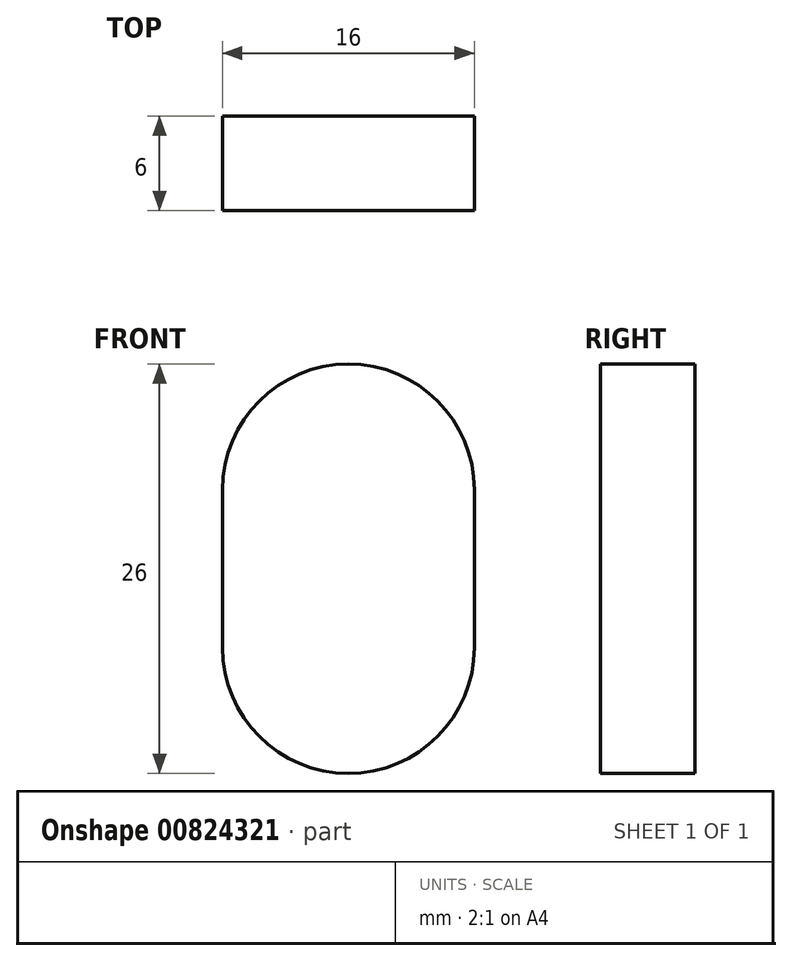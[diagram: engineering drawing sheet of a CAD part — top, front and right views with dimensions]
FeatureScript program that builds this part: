
annotation { "Feature Type Name" : "Feature", "Feature Type Description" : "" }
export const myFeature = defineFeature(function(context is Context, id is Id, definition is map)
    precondition{}
    {
        {
            var Q0;
            Q0=qCreatedBy(makeId("Front.planeOp"),FACE);
            var sketch = newSketch(context, id + "F0", { "sketchPlane" : qUnion([Q0])});
            skLineSegment(sketch, "E0.bottom", {"start": v(130, 80) * mm, "end": v(-130, 80) * mm});
            skLineSegment(sketch, "E0.top", {"start": v(130, -80) * mm, "end": v(-130, -80) * mm});
            skLineSegment(sketch, "E0.left", {"start": v(130, 80) * mm, "end": v(130, -80) * mm});
            skLineSegment(sketch, "E0.right", {"start": v(-130, 80) * mm, "end": v(-130, -80) * mm});
            skPoint(sketch, "E0.middle", {"position": v(0, 0) * mm});
            skSolve(sketch);
        }
        {
            var Q0;
            Q0=makeQuery(id+"F0.imprint","IMPRINT",FACE,{"disambiguationData":[TD([[makeQuery(id+"F0.imprint","IMPRINT",EDGE,{"derivedFrom":sQuery(id+"F0.wireOp",EDGE,"E0.bottom")}),1.0]])]});
            extrude(context, id + "F1", {"entities" : qUnion([Q0]), "depth" : 6 * mm, "offsetDistance" : 25 * mm});
        }
        {
            var Q0;
            Q0=makeQuery(id+"F1.opExtrude","CAP_FACE",FACE,{"disambiguationData":[OSD([sQuery(id+"F0.wireOp",EDGE,"E0.bottom"),sQuery(id+"F0.wireOp",EDGE,"E0.top"),sQuery(id+"F0.wireOp",EDGE,"E0.left"),sQuery(id+"F0.wireOp",EDGE,"E0.right")])],"isStart":false});
            var sketch = newSketch(context, id + "F2", { "sketchPlane" : qUnion([Q0])});
            skLineSegment(sketch, "E1.bottom", {"start": v(-110, -13) * mm, "end": v(-110, -13) * mm});
            skLineSegment(sketch, "E1.top", {"start": v(-110, 13) * mm, "end": v(-110, 13) * mm});
            skLineSegment(sketch, "E1.left", {"start": v(-102, -5) * mm, "end": v(-102, 5) * mm});
            skLineSegment(sketch, "E1.right", {"start": v(-118, -5) * mm, "end": v(-118, 5) * mm});
            skPoint(sketch, "E1.middle", {"position": v(-110, 0) * mm});
            skPoint(sketch, "E2.visualSharp", {"position": v(-118, 13) * mm});
            skArc(sketch, "E2.filletArc", {"start": v(-110, 13) * mm, "mid": v(-115.66, 10.66) * mm, "end": v(-118, 5) * mm});
            skPoint(sketch, "E3.visualSharp", {"position": v(-102, 13) * mm});
            skArc(sketch, "E3.filletArc", {"start": v(-102, 5) * mm, "mid": v(-104.34, 10.66) * mm, "end": v(-110, 13) * mm});
            skPoint(sketch, "E4.visualSharp", {"position": v(-102, -13) * mm});
            skArc(sketch, "E4.filletArc", {"start": v(-110, -13) * mm, "mid": v(-104.34, -10.66) * mm, "end": v(-102, -5) * mm});
            skPoint(sketch, "E5.visualSharp", {"position": v(-118, -13) * mm});
            skArc(sketch, "E5.filletArc", {"start": v(-118, -5) * mm, "mid": v(-115.66, -10.66) * mm, "end": v(-110, -13) * mm});
            skArc(sketch, "E6.MirrorCS", {"start": v(118, -5) * mm, "mid": v(115.66, -10.66) * mm, "end": v(110, -13) * mm});
            skArc(sketch, "E7.MirrorCS", {"start": v(110, -13) * mm, "mid": v(104.34, -10.66) * mm, "end": v(102, -5) * mm});
            skArc(sketch, "E8.MirrorCS", {"start": v(102, 5) * mm, "mid": v(104.34, 10.66) * mm, "end": v(110, 13) * mm});
            skArc(sketch, "E9.MirrorCS", {"start": v(110, 13) * mm, "mid": v(115.66, 10.66) * mm, "end": v(118, 5) * mm});
            skPoint(sketch, "E10.MirrorP", {"position": v(110, 0) * mm});
            skLineSegment(sketch, "E11.MirrorCS", {"start": v(102, -5) * mm, "end": v(102, 5) * mm});
            skLineSegment(sketch, "E12.MirrorCS", {"start": v(118, -5) * mm, "end": v(118, 5) * mm});
            skPoint(sketch, "E13.MirrorP", {"position": v(102, 13) * mm});
            skPoint(sketch, "E14.MirrorP", {"position": v(102, -13) * mm});
            skPoint(sketch, "E15.MirrorP", {"position": v(118, -13) * mm});
            skPoint(sketch, "E16.MirrorP", {"position": v(118, 13) * mm});
            skSolve(sketch);
        }
        {
            var Q0;
            Q0=makeQuery(id+"F2.imprint","IMPRINT",FACE,{"disambiguationData":[TD([[makeQuery(id+"F2.imprint","IMPRINT",EDGE,{"derivedFrom":sQuery(id+"F2.wireOp",EDGE,"E1.left")}),1.0]])]});
            var Q1;
            Q1=makeQuery(id+"F2.imprint","IMPRINT",FACE,{"disambiguationData":[TD([[makeQuery(id+"F2.imprint","IMPRINT",EDGE,{"derivedFrom":sQuery(id+"F2.wireOp",EDGE,"E6.MirrorCS")}),-1.0]])]});
            extrude(context, id + "F3", {"entities" : qUnion([Q0, Q1]), "operationType" : NewBodyOperationType.REMOVE, "endBound" : BoundingType.THROUGH_ALL, "oppositeDirection" : true, "depth" : 25 * mm, "offsetDistance" : 25 * mm});
        }
    });
